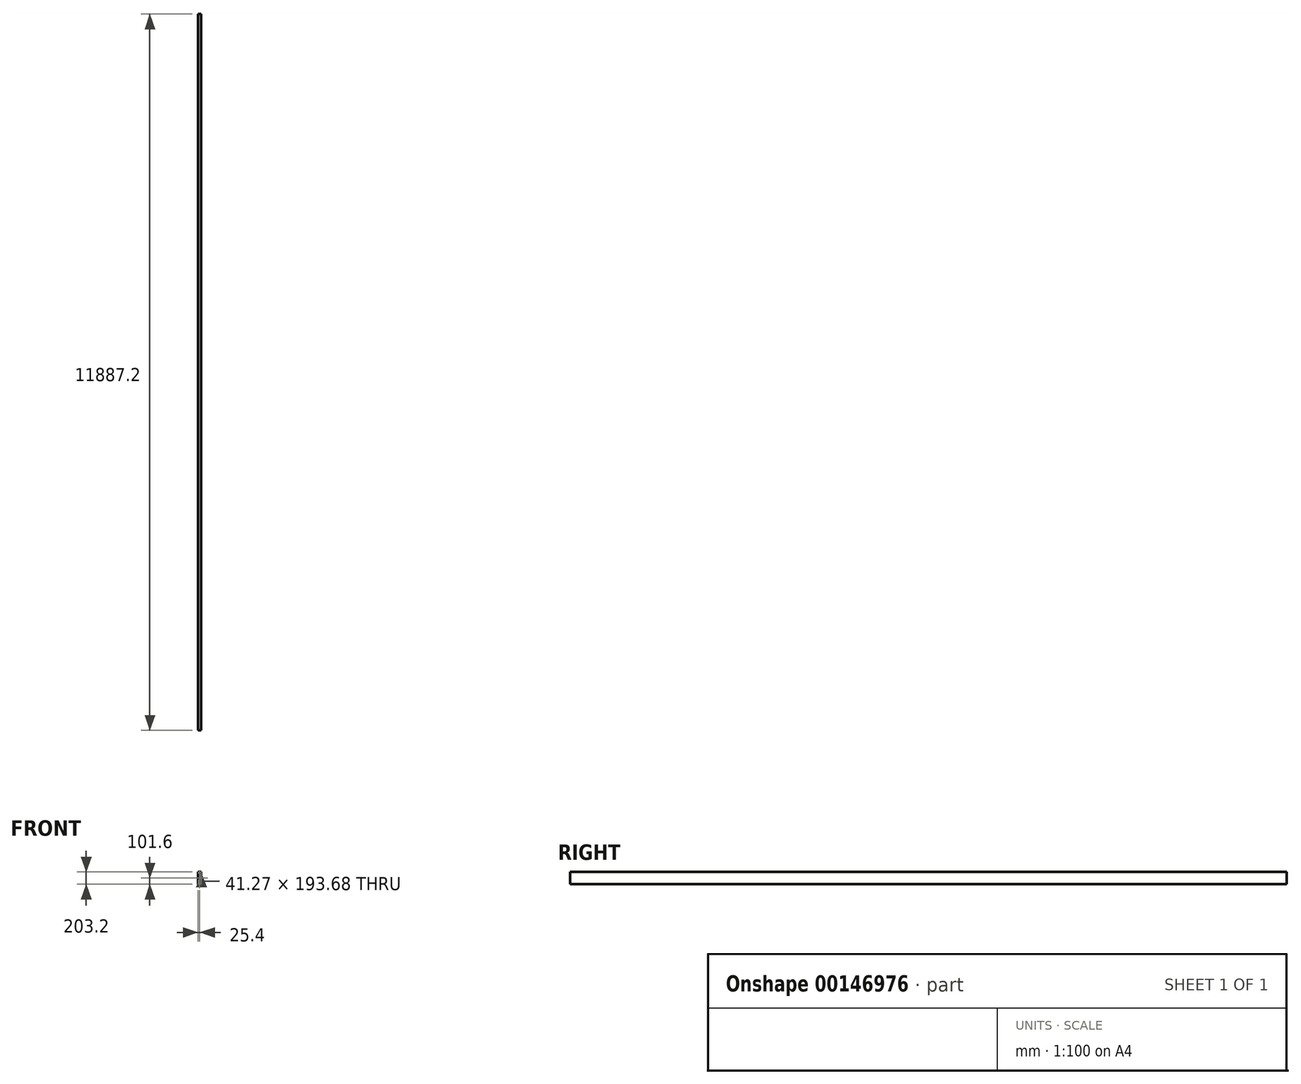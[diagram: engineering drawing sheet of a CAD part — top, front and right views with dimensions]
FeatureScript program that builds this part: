
annotation { "Feature Type Name" : "Feature", "Feature Type Description" : "" }
export const myFeature = defineFeature(function(context is Context, id is Id, definition is map)
    precondition{}
    {
        {
            var Q0;
            Q0=qCreatedBy(makeId("Front.planeOp"),FACE);
            var sketch = newSketch(context, id + "F0", { "sketchPlane" : qUnion([Q0])});
            skLineSegment(sketch, "E0.bottom", {"start": v(0, 0) * mm, "end": v(50.8, 0) * mm});
            skLineSegment(sketch, "E0.top", {"start": v(0, 203.2) * mm, "end": v(50.8, 203.2) * mm});
            skLineSegment(sketch, "E0.left", {"start": v(0, 0) * mm, "end": v(0, 203.2) * mm});
            skLineSegment(sketch, "E0.right", {"start": v(50.8, 0) * mm, "end": v(50.8, 203.2) * mm});
            skLineSegment(sketch, "E1.bottom", {"start": v(4.76, 198.44) * mm, "end": v(46.04, 198.44) * mm});
            skLineSegment(sketch, "E1.top", {"start": v(4.76, 4.76) * mm, "end": v(46.04, 4.76) * mm});
            skLineSegment(sketch, "E1.left", {"start": v(4.76, 198.44) * mm, "end": v(4.76, 4.76) * mm});
            skLineSegment(sketch, "E1.right", {"start": v(46.04, 198.44) * mm, "end": v(46.04, 4.76) * mm});
            skSolve(sketch);
        }
        {
            var Q0;
            Q0=makeQuery(id+"F0.imprint","IMPRINT",FACE,{"disambiguationData":[TD([[makeQuery(id+"F0.imprint","IMPRINT",EDGE,{"derivedFrom":sQuery(id+"F0.wireOp",EDGE,"E0.bottom")}),1.0]])]});
            extrude(context, id + "F1", {"entities" : qUnion([Q0]), "oppositeDirection" : true, "depth" : 11887.2 * mm});
        }
    });
